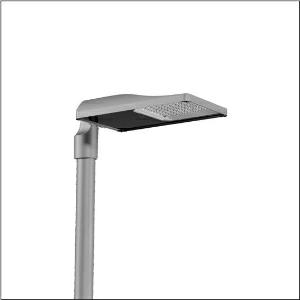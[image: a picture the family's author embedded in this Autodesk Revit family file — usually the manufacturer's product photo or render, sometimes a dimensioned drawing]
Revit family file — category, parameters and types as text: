
# Revit family: streetlight_sl_31_midi___pl52_5xh3h4aa08ma_de42
name_source: partatom
category: Lighting Fixtures
units: mm (PartAtom-declared; Revit-internal decimal feet)

## family parameters
Cut with Voids When Loaded = No
Host = Face
Light Source = No
Part Type = Normal
Room Calculation Point = No
Round Connector Dimension = Use Diameter
Shared = No

## types (1)
- --- (1 x LED, 19840 lm, 145.3 W, 4000K)
    Apparent Load = 145 VA
    CIE Flux Codes = 27 59 98 100 100
    Color Rendering = 70
    Color Temperature = 4000K
    Default Elevation = 1800 mm
    Description = Streetlight SL 31 midi Easy mast luminaire for post-top, side-entry; light control with lens of PMMA; light distribution: PL52, direct asymmetric distribution, for standard-compliant lighting for roads and squares; LED: luminous flux: 19.840lm, light colour: 740, colour temperature: 4000K; luminous efficacy: 136,5lm/W; control: pre-setting: linear dimming characteristic, flexible luminous flux parameterisation, time-dependent luminous flux control, constant luminous flux control, power reduction, intelligent temperature release in ECG and LED module, overheat protection; luminaire housing, of diecast aluminium, SITECO metallic grey (DB 702S), corrosivity category C5 high according to DIN EN ISO 12944; cover of toughened safety glass, transparent, mast flange of diecast aluminium, SITECO metallic grey (DB 702S), spigot size: 76/60mm, mast flange included unmounted; with cable H07RN-F 3x 1.5mm², cable length: 10,5m, connection cable pre-assembled; mains connection: 220..240V, AC, 50/60Hz; power consumption (at start of service life): 145,3W / (at end of service life): 161,8W / (with reduced operation 50%): 61,1W; protection rating (complete): IP66; insulation class (complete): insulation class II (safety insulation); impact resistance: IK10; certification: CE, ENEC, ENEC+, VDE, UKCA; permissible operating ambient temperature for outdoor applications: -40..+50°C; packaging unit: 1 piece

Light Distribution: PL52
    Height = 79 mm
    Lamp = 1 x LED
    Lamp Light Flux = 19840 lm
    Lamp Power = 145.3 W
    Lamp count = 1
    Length = 577 mm
    Luminous efficacy = 137 lm/W
    Manufacturer = Siteco
    ModVariant = No
    Model = 5XH3H4AA08MA
    Mounting Place = Pole
    Mounting Type = Pole top
    Number of Poles = 1
    OnlyDefault = Yes
    Power Factor = 1
    Product Name = Streetlight SL 31 midi | PL52
    Product group = mast luminaire | pylon top
    ProductGroupID = 6100
    Protection Class = Protection class II
    Protection Degree = IP 66
    RLX_Detail_Level = 1
    RLX_Emergency_Light_Flux = 0 lm
    RLX_Emergency_Type = 0
    RLX_Emergency_Type_DB = No
    RlxData = <blob elided: 52353 chars, md5=9da726f2>
    Socket = socket
    Standby Power = 0 W
    System Light Flux = 19841 lm
    System Power = 145 W
    Type Comments = factory setting: luminous flux: 100 % | dim-lin: 254 | 747 mA
    Type Image = l_1300317.jpg
    URL = http://relux.com
    VarID = @adj_051953
    Voltage = 0 V
    Weight = 0.00 kg
    Width = 362 mm

## geometry (parser evidence)
native form markers: Blend x4, Sweep x14
no freeform markers — native parametric forms only
